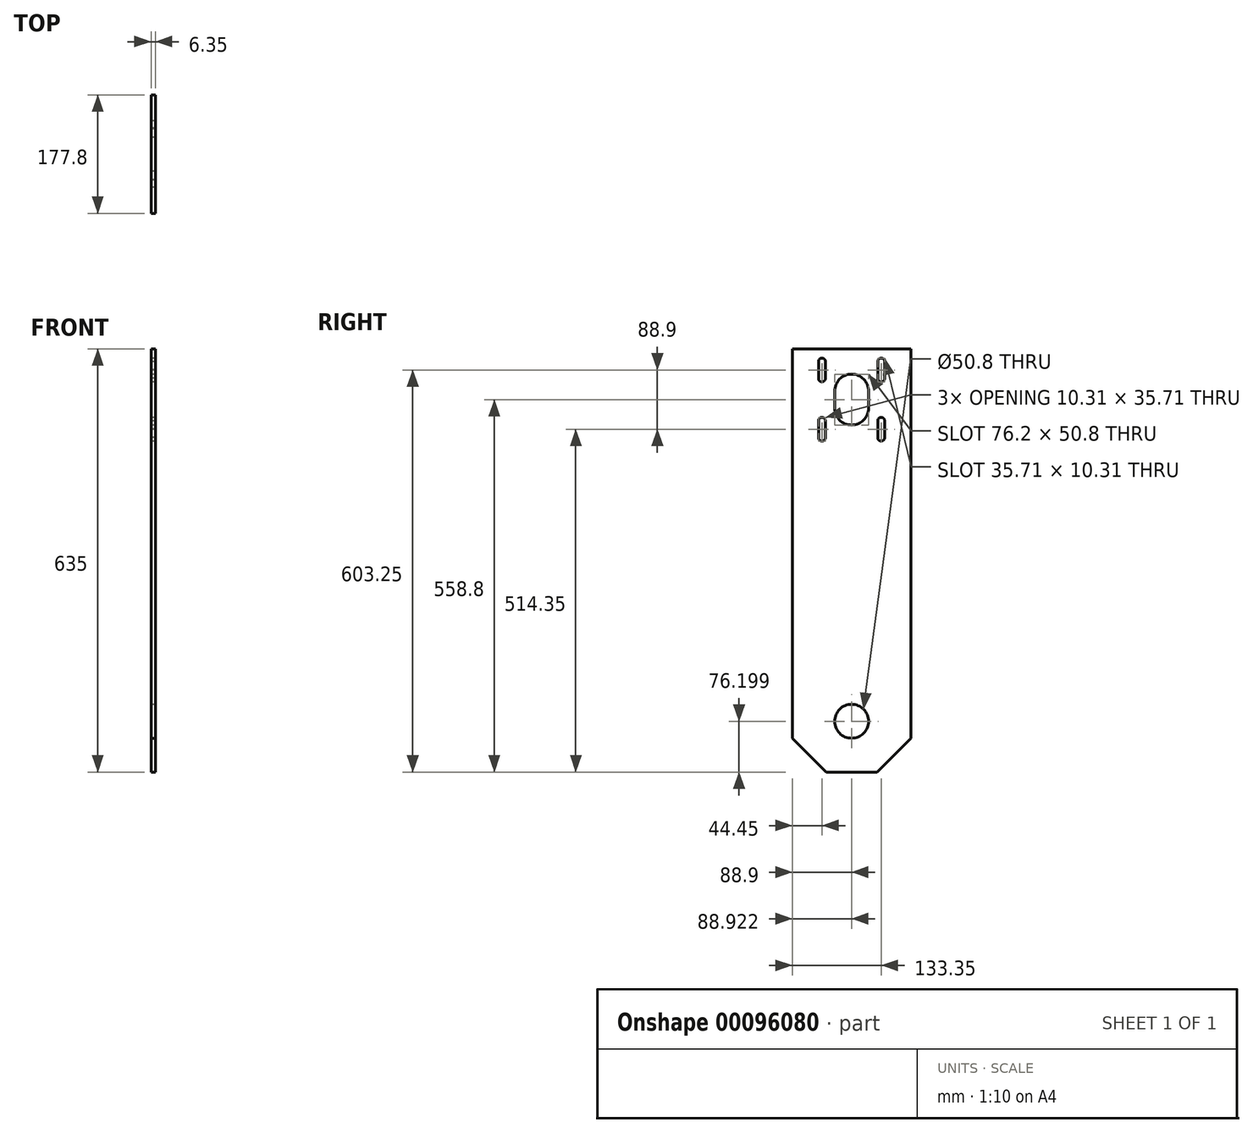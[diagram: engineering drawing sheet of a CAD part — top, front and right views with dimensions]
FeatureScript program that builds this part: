
annotation { "Feature Type Name" : "Feature", "Feature Type Description" : "" }
export const myFeature = defineFeature(function(context is Context, id is Id, definition is map)
    precondition{}
    {
        {
            var Q0;
            Q0=qCreatedBy(makeId("Right.planeOp"),FACE);
            var sketch = newSketch(context, id + "F0", { "sketchPlane" : qUnion([Q0])});
            skLineSegment(sketch, "E0.top", {"start": v(-88.9, 292.1) * mm, "end": v(88.9, 292.1) * mm});
            skLineSegment(sketch, "E0.left", {"start": v(-88.9, -292.1) * mm, "end": v(-88.9, 292.1) * mm});
            skLineSegment(sketch, "E0.right", {"start": v(88.9, -292.1) * mm, "end": v(88.9, 292.1) * mm});
            skPoint(sketch, "E0.middle", {"position": v(0, 0) * mm});
            skLineSegment(sketch, "E1", {"start": v(-88.9, -292.1) * mm, "end": v(-38.1, -342.9) * mm});
            skLineSegment(sketch, "E2", {"start": v(-38.1, -342.9) * mm, "end": v(38.1, -342.9) * mm});
            skLineSegment(sketch, "E3", {"start": v(38.1, -342.9) * mm, "end": v(88.9, -292.1) * mm});
            skLineSegment(sketch, "E4", {"start": v(0, 292.1) * mm, "end": v(0, 215.9) * mm});
            skLineSegment(sketch, "E5", {"start": v(0, -342.9) * mm, "end": v(0, -266.7) * mm});
            skPoint(sketch, "E5.endSnap0", {"position": v(0, -342.9) * mm});
            skLineSegment(sketch, "E6", {"start": v(0, 215.9) * mm, "end": v(0, 228.6) * mm, "construction": true});
            skLineSegment(sketch, "E7", {"start": v(0, 215.9) * mm, "end": v(0, 203.2) * mm, "construction": true});
            skCircle(sketch, "E8", {"center": v(0, 228.6) * mm, "radius": 25.4 * mm});
            skCircle(sketch, "E9", {"center": v(0, 203.2) * mm, "radius": 25.4 * mm});
            skLineSegment(sketch, "E10", {"start": v(25.4, 228.6) * mm, "end": v(25.4, 203.2) * mm});
            skLineSegment(sketch, "E11", {"start": v(-25.4, 228.6) * mm, "end": v(-25.4, 203.2) * mm});
            skCircle(sketch, "E12", {"center": v(-44.45, 260.35) * mm, "radius": 5.16 * mm});
            skCircle(sketch, "E13", {"center": v(44.45, 171.45) * mm, "radius": 5.16 * mm});
            skCircle(sketch, "E14", {"center": v(-44.45, 171.45) * mm, "radius": 5.16 * mm});
            skCircle(sketch, "E15", {"center": v(-44.45, 247.65) * mm, "radius": 5.16 * mm});
            skCircle(sketch, "E16", {"center": v(-44.45, 273.05) * mm, "radius": 5.16 * mm});
            skCircle(sketch, "E17", {"center": v(-44.45, 184.15) * mm, "radius": 5.16 * mm});
            skCircle(sketch, "E18", {"center": v(-44.45, 158.75) * mm, "radius": 5.16 * mm});
            skCircle(sketch, "E19", {"center": v(44.45, 273.05) * mm, "radius": 5.16 * mm});
            skCircle(sketch, "E20", {"center": v(44.45, 247.65) * mm, "radius": 5.16 * mm});
            skCircle(sketch, "E21", {"center": v(44.45, 184.15) * mm, "radius": 5.16 * mm});
            skCircle(sketch, "E22", {"center": v(44.45, 158.75) * mm, "radius": 5.16 * mm});
            skCircle(sketch, "E23", {"center": v(44.45, 260.35) * mm, "radius": 5.16 * mm});
            skLineSegment(sketch, "E24", {"start": v(39.3, 273.05) * mm, "end": v(39.3, 247.65) * mm});
            skLineSegment(sketch, "E25", {"start": v(49.6, 273.05) * mm, "end": v(49.6, 247.65) * mm});
            skLineSegment(sketch, "E26", {"start": v(39.3, 184.1) * mm, "end": v(39.3, 158.8) * mm});
            skLineSegment(sketch, "E27", {"start": v(49.6, 184.2) * mm, "end": v(49.6, 158.8) * mm});
            skLineSegment(sketch, "E28", {"start": v(-39.3, 184.17) * mm, "end": v(-39.3, 158.77) * mm});
            skLineSegment(sketch, "E29", {"start": v(-49.6, 183.92) * mm, "end": v(-49.6, 158.52) * mm});
            skLineSegment(sketch, "E30", {"start": v(-49.6, 272.94) * mm, "end": v(-49.6, 247.65) * mm});
            skLineSegment(sketch, "E31", {"start": v(-39.3, 273.21) * mm, "end": v(-39.3, 247.49) * mm});
            skCircle(sketch, "E32", {"center": v(0.02, -266.7) * mm, "radius": 25.4 * mm});
            skSolve(sketch);
        }
        {
            var Q0;
            {var subQ1=sQuery(id+"F0.wireOp",EDGE,"E0.left");Q0=makeQuery(id+"F0.imprint","IMPRINT",FACE,{"disambiguationData":[TD([[makeQuery(id+"F0.imprint","IMPRINT",EDGE,{"derivedFrom":subQ1}),-1.0]])]});}
            extrude(context, id + "F1", {"entities" : qUnion([Q0]), "depth" : 6.35 * mm});
        }
    });
